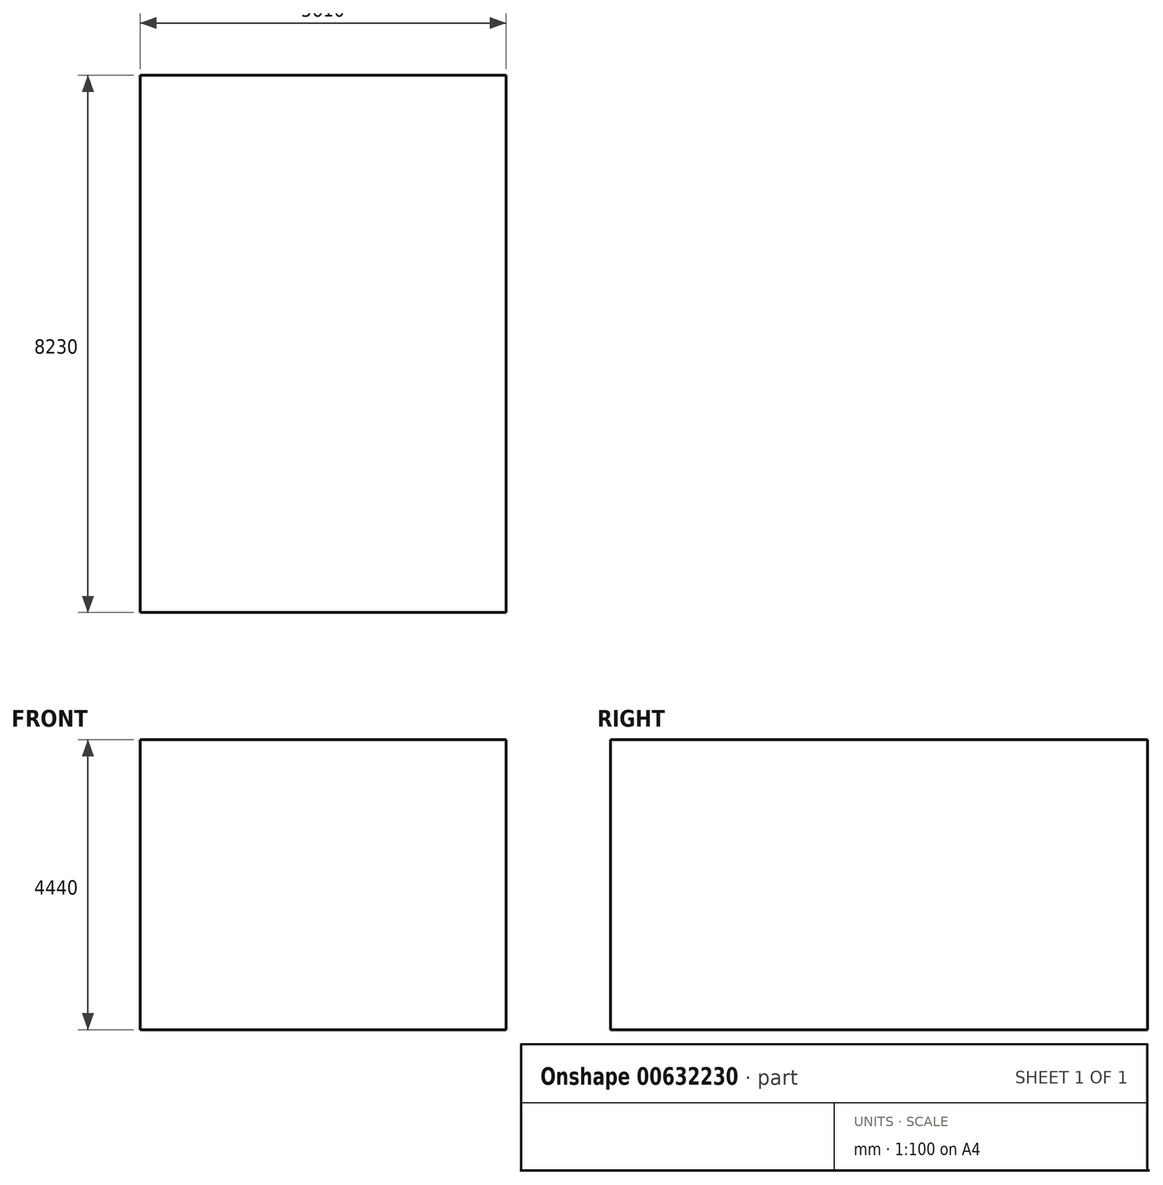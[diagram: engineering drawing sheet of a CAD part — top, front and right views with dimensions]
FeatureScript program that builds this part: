
annotation { "Feature Type Name" : "Feature", "Feature Type Description" : "" }
export const myFeature = defineFeature(function(context is Context, id is Id, definition is map)
    precondition{}
    {
        {
            var Q0;
            Q0=qCreatedBy(makeId("Front.planeOp"),FACE);
            var sketch = newSketch(context, id + "F0", { "sketchPlane" : qUnion([Q0])});
            skLineSegment(sketch, "E0.bottom", {"start": v(0, -2901.57) * mm, "end": v(5610, -2901.57) * mm});
            skLineSegment(sketch, "E0.top", {"start": v(0, 1538.43) * mm, "end": v(5610, 1538.43) * mm});
            skLineSegment(sketch, "E0.left", {"start": v(0, -2901.57) * mm, "end": v(0, 1538.43) * mm});
            skLineSegment(sketch, "E0.right", {"start": v(5610, -2901.57) * mm, "end": v(5610, 1538.43) * mm});
            skSolve(sketch);
        }
        {
            var Q0;
            Q0=qSketchRegion(id+"F0",true);
            extrude(context, id + "F1", {"entities" : qUnion([Q0]), "depth" : 8230 * mm, "offsetDistance" : 25.4 * mm});
        }
    });
